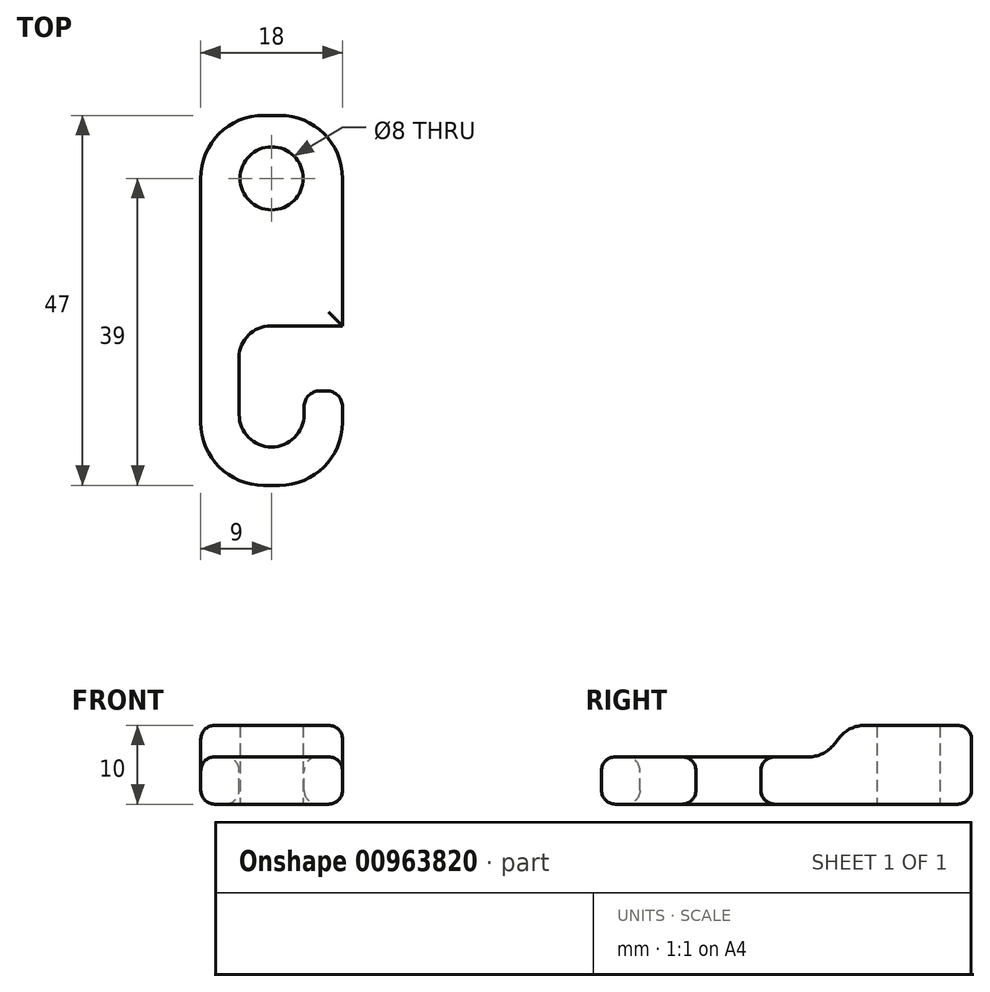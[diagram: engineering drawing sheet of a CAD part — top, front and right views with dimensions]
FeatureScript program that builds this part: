
annotation { "Feature Type Name" : "Feature", "Feature Type Description" : "" }
export const myFeature = defineFeature(function(context is Context, id is Id, definition is map)
    precondition{}
    {
        {
            var Q0;
            Q0=qCreatedBy(makeId("Top.planeOp"),FACE);
            var sketch = newSketch(context, id + "F0", { "sketchPlane" : qUnion([Q0])});
            skLineSegment(sketch, "E0.bottom", {"start": v(-9, 38) * mm, "end": v(9, 38) * mm});
            skLineSegment(sketch, "E0.top", {"start": v(-9, -9) * mm, "end": v(9, -9) * mm});
            skLineSegment(sketch, "E0.left", {"start": v(-9, 38) * mm, "end": v(-9, -9) * mm});
            skLineSegment(sketch, "E0.right", {"start": v(9, 38) * mm, "end": v(9, -9) * mm});
            skLineSegment(sketch, "E1", {"start": v(0, 38) * mm, "end": v(0, -9) * mm, "construction": true});
            skCircle(sketch, "E2", {"center": v(0, 30) * mm, "radius": 4 * mm});
            skSolve(sketch);
        }
        {
            var Q0;
            Q0 = qSketchRegion(id + "F0", true);
            extrude(context, id + "F1", {"entities" : qUnion([Q0]), "depth" : 10 * mm, "offsetDistance" : 25 * mm});
        }
        {
            var Q0;
            Q0=makeQuery(id+"F1.opExtrude","CAP_FACE",FACE,{"disambiguationData":[OSD([sQuery(id+"F0.wireOp",EDGE,"E0.bottom"),sQuery(id+"F0.wireOp",EDGE,"E0.top"),sQuery(id+"F0.wireOp",EDGE,"E0.left"),sQuery(id+"F0.wireOp",EDGE,"E0.right"),sQuery(id+"F0.wireOp",EDGE,"E2")])],"isStart":false});
            var sketch = newSketch(context, id + "F2", { "sketchPlane" : qUnion([Q0])});
            skArc(sketch, "E3", {"start": v(-4.13, 0) * mm, "mid": v(0, -4.13) * mm, "end": v(4.13, 0) * mm});
            skLineSegment(sketch, "E4", {"start": v(0, 32.94) * mm, "end": v(0, -9) * mm, "construction": true});
            skLineSegment(sketch, "E5", {"start": v(-4.13, 0) * mm, "end": v(-4.13, 7.25) * mm});
            skLineSegment(sketch, "E6", {"start": v(4.12, 0) * mm, "end": v(4.12, 3) * mm});
            skLineSegment(sketch, "E7", {"start": v(9, 11.25) * mm, "end": v(-0.13, 11.25) * mm});
            skLineSegment(sketch, "E8", {"start": v(4.12, 3) * mm, "end": v(9, 3) * mm});
            skLineSegment(sketch, "E9", {"start": v(9, 11.25) * mm, "end": v(9, 3) * mm});
            skPoint(sketch, "E10.visualSharp", {"position": v(-4.13, 11.25) * mm});
            skArc(sketch, "E10.filletArc", {"start": v(-0.13, 11.25) * mm, "mid": v(-2.95, 10.08) * mm, "end": v(-4.13, 7.25) * mm});
            skSolve(sketch);
        }
        {
            var Q0;
            Q0 = qSketchRegion(id + "F2", true);
            extrude(context, id + "F3", {"entities" : qUnion([Q0]), "operationType" : NewBodyOperationType.REMOVE, "endBound" : BoundingType.UP_TO_NEXT, "oppositeDirection" : true, "depth" : 25 * mm, "offsetDistance" : 25 * mm});
        }
        {
            var Q0;
            Q0=makeQuery(id+"F3.boolean.opBoolean","COPY",EDGE,{"derivedFrom":makeQuery(id+"F3.opExtrude","SWEPT_EDGE",EDGE,{"disambiguationData":[OSD([sQuery(id+"F0.wireOp",EDGE,"E0.right"),sQuery(id+"F2.wireOp",EDGE,"E7"),sQuery(id+"F2.wireOp",EDGE,"E9")])]})});
            var Q1;
            Q1=makeQuery(id+"F3.boolean.opBoolean","COPY",EDGE,{"derivedFrom":makeQuery(id+"F3.opExtrude","SWEPT_EDGE",EDGE,{"disambiguationData":[OSD([sQuery(id+"F2.wireOp",EDGE,"E6"),sQuery(id+"F2.wireOp",EDGE,"E8")])]})});
            var Q2;
            Q2=makeQuery(id+"F3.boolean.opBoolean","COPY",EDGE,{"derivedFrom":makeQuery(id+"F3.opExtrude","SWEPT_EDGE",EDGE,{"disambiguationData":[OSD([sQuery(id+"F0.wireOp",EDGE,"E0.right"),sQuery(id+"F2.wireOp",EDGE,"E8"),sQuery(id+"F2.wireOp",EDGE,"E9")])]})});
            fillet(context, id + "F4", {"entities" : qUnion([Q0, Q1, Q2]), "radius" : 2 * mm, "tangentPropagation" : true, "allowEdgeOverflow" : false});
        }
        {
            var Q0;
            Q0=makeQuery(id+"F1.opExtrude","SWEPT_EDGE",EDGE,{"disambiguationData":[OSD([sQuery(id+"F0.wireOp",EDGE,"E0.bottom"),sQuery(id+"F0.wireOp",EDGE,"E0.left")])]});
            var Q1;
            Q1=makeQuery(id+"F1.opExtrude","SWEPT_EDGE",EDGE,{"disambiguationData":[OSD([sQuery(id+"F0.wireOp",EDGE,"E0.bottom"),sQuery(id+"F0.wireOp",EDGE,"E0.right")])]});
            var Q2;
            Q2=makeQuery(id+"F1.opExtrude","SWEPT_EDGE",EDGE,{"disambiguationData":[OSD([sQuery(id+"F0.wireOp",EDGE,"E0.top"),sQuery(id+"F0.wireOp",EDGE,"E0.right")])]});
            var Q3;
            Q3=makeQuery(id+"F1.opExtrude","SWEPT_EDGE",EDGE,{"disambiguationData":[OSD([sQuery(id+"F0.wireOp",EDGE,"E0.top"),sQuery(id+"F0.wireOp",EDGE,"E0.left")])]});
            fillet(context, id + "F5", {"entities" : qUnion([Q0, Q1, Q2, Q3]), "radius" : 8 * mm, "tangentPropagation" : true, "allowEdgeOverflow" : false});
        }
        {
            var Q0;
            Q0=qCreatedBy(makeId("Right.planeOp"),FACE);
            cPlane(context, id + "F6", {"entities" : qUnion([Q0]), "cplaneType" : CPlaneType.OFFSET, "offset" : 31.1 * mm, "width" : 150 * mm, "height" : 150 * mm});
        }
        {
            var Q0;
            Q0=qCreatedBy(id+"F6.planeOp",FACE);
            var sketch = newSketch(context, id + "F7", { "sketchPlane" : qUnion([Q0])});
            skLineSegment(sketch, "E11", {"start": v(-18.77, 6) * mm, "end": v(19.18, 6) * mm});
            skLineSegment(sketch, "E12", {"start": v(19.18, 6) * mm, "end": v(28.14, 16.65) * mm});
            skLineSegment(sketch, "E13", {"start": v(28.14, 16.65) * mm, "end": v(-19.33, 16.65) * mm});
            skLineSegment(sketch, "E14", {"start": v(-19.33, 16.65) * mm, "end": v(-18.77, 6) * mm});
            skSolve(sketch);
        }
        {
            var Q0;
            Q0 = qSketchRegion(id + "F7", true);
            extrude(context, id + "F8", {"entities" : qUnion([Q0]), "operationType" : NewBodyOperationType.REMOVE, "endBound" : BoundingType.THROUGH_ALL, "oppositeDirection" : true, "depth" : 25 * mm, "offsetDistance" : 25 * mm});
        }
        {
            var Q0;
            Q0=makeQuery(id+"F8.boolean.opBoolean","INTERSECT",EDGE,{"derivedFrom":[makeQuery(id+"F1.opExtrude","CAP_FACE",FACE,{"disambiguationData":[OSD([sQuery(id+"F0.wireOp",EDGE,"E0.bottom"),sQuery(id+"F0.wireOp",EDGE,"E0.top"),sQuery(id+"F0.wireOp",EDGE,"E0.left"),sQuery(id+"F0.wireOp",EDGE,"E0.right"),sQuery(id+"F0.wireOp",EDGE,"E2")])],"isStart":false}),makeQuery(id+"F8.opExtrude","SWEPT_FACE",FACE,{"disambiguationData":[OSD([sQuery(id+"F7.wireOp",EDGE,"E12")])]})]});
            var Q1;
            Q1=makeQuery(id+"F8.boolean.opBoolean","COPY",EDGE,{"derivedFrom":makeQuery(id+"F8.opExtrude","SWEPT_EDGE",EDGE,{"disambiguationData":[OSD([sQuery(id+"F7.wireOp",EDGE,"E11"),sQuery(id+"F7.wireOp",EDGE,"E12")])]})});
            fillet(context, id + "F9", {"entities" : qUnion([Q0, Q1]), "radius" : 4 * mm, "tangentPropagation" : true, "allowEdgeOverflow" : false});
        }
        {
            var Q0;
            {var subQ0=sQuery(id+"F0.wireOp",EDGE,"E0.left");var subQ1=sQuery(id+"F0.wireOp",EDGE,"E0.bottom");Q0=makeQuery(id+"F5.opFillet","BLEND_EDGE",EDGE,{"blendedFrom":[makeQuery(id+"F1.opExtrude","SWEPT_EDGE",EDGE,{"disambiguationData":[OSD([subQ1,subQ0])]}),makeQuery(id+"F1.opExtrude","CAP_FACE",FACE,{"disambiguationData":[OSD([subQ1,sQuery(id+"F0.wireOp",EDGE,"E0.top"),subQ0,sQuery(id+"F0.wireOp",EDGE,"E0.right"),sQuery(id+"F0.wireOp",EDGE,"E2")])],"isStart":false})],"blendedInto":[makeQuery(id+"F1.opExtrude","CAP_FACE",FACE,{"disambiguationData":[OSD([subQ1,sQuery(id+"F0.wireOp",EDGE,"E0.top"),subQ0,sQuery(id+"F0.wireOp",EDGE,"E0.right"),sQuery(id+"F0.wireOp",EDGE,"E2")])],"isStart":false})]});}
            var Q1;
            {var subQ0=sQuery(id+"F0.wireOp",EDGE,"E0.right");var subQ1=sQuery(id+"F0.wireOp",EDGE,"E0.bottom");Q1=makeQuery(id+"F5.opFillet","BLEND_EDGE",EDGE,{"blendedFrom":[makeQuery(id+"F1.opExtrude","SWEPT_EDGE",EDGE,{"disambiguationData":[OSD([subQ1,subQ0])]}),makeQuery(id+"F1.opExtrude","CAP_FACE",FACE,{"disambiguationData":[OSD([subQ1,sQuery(id+"F0.wireOp",EDGE,"E0.top"),sQuery(id+"F0.wireOp",EDGE,"E0.left"),subQ0,sQuery(id+"F0.wireOp",EDGE,"E2")])],"isStart":false})],"blendedInto":[makeQuery(id+"F1.opExtrude","CAP_FACE",FACE,{"disambiguationData":[OSD([subQ1,sQuery(id+"F0.wireOp",EDGE,"E0.top"),sQuery(id+"F0.wireOp",EDGE,"E0.left"),subQ0,sQuery(id+"F0.wireOp",EDGE,"E2")])],"isStart":false})]});}
            var Q2;
            {var subQ0=sQuery(id+"F0.wireOp",EDGE,"E0.left");var subQ1=sQuery(id+"F0.wireOp",EDGE,"E0.bottom");Q2=makeQuery(id+"F5.opFillet","BLEND_EDGE",EDGE,{"blendedFrom":[makeQuery(id+"F1.opExtrude","SWEPT_EDGE",EDGE,{"disambiguationData":[OSD([subQ1,subQ0])]}),makeQuery(id+"F1.opExtrude","CAP_FACE",FACE,{"disambiguationData":[OSD([subQ1,sQuery(id+"F0.wireOp",EDGE,"E0.top"),subQ0,sQuery(id+"F0.wireOp",EDGE,"E0.right"),sQuery(id+"F0.wireOp",EDGE,"E2")])],"isStart":true})],"blendedInto":[makeQuery(id+"F1.opExtrude","CAP_FACE",FACE,{"disambiguationData":[OSD([subQ1,sQuery(id+"F0.wireOp",EDGE,"E0.top"),subQ0,sQuery(id+"F0.wireOp",EDGE,"E0.right"),sQuery(id+"F0.wireOp",EDGE,"E2")])],"isStart":true})]});}
            var Q3;
            {var subQ0=sQuery(id+"F0.wireOp",EDGE,"E0.right");var subQ1=sQuery(id+"F0.wireOp",EDGE,"E0.bottom");Q3=makeQuery(id+"F5.opFillet","BLEND_EDGE",EDGE,{"blendedFrom":[makeQuery(id+"F1.opExtrude","SWEPT_EDGE",EDGE,{"disambiguationData":[OSD([subQ1,subQ0])]}),makeQuery(id+"F1.opExtrude","CAP_FACE",FACE,{"disambiguationData":[OSD([subQ1,sQuery(id+"F0.wireOp",EDGE,"E0.top"),sQuery(id+"F0.wireOp",EDGE,"E0.left"),subQ0,sQuery(id+"F0.wireOp",EDGE,"E2")])],"isStart":true})],"blendedInto":[makeQuery(id+"F1.opExtrude","CAP_FACE",FACE,{"disambiguationData":[OSD([subQ1,sQuery(id+"F0.wireOp",EDGE,"E0.top"),sQuery(id+"F0.wireOp",EDGE,"E0.left"),subQ0,sQuery(id+"F0.wireOp",EDGE,"E2")])],"isStart":true})]});}
            fillet(context, id + "F10", {"entities" : qUnion([Q0, Q1, Q2, Q3]), "radius" : 1.75 * mm, "tangentPropagation" : true, "allowEdgeOverflow" : false});
        }
    });
